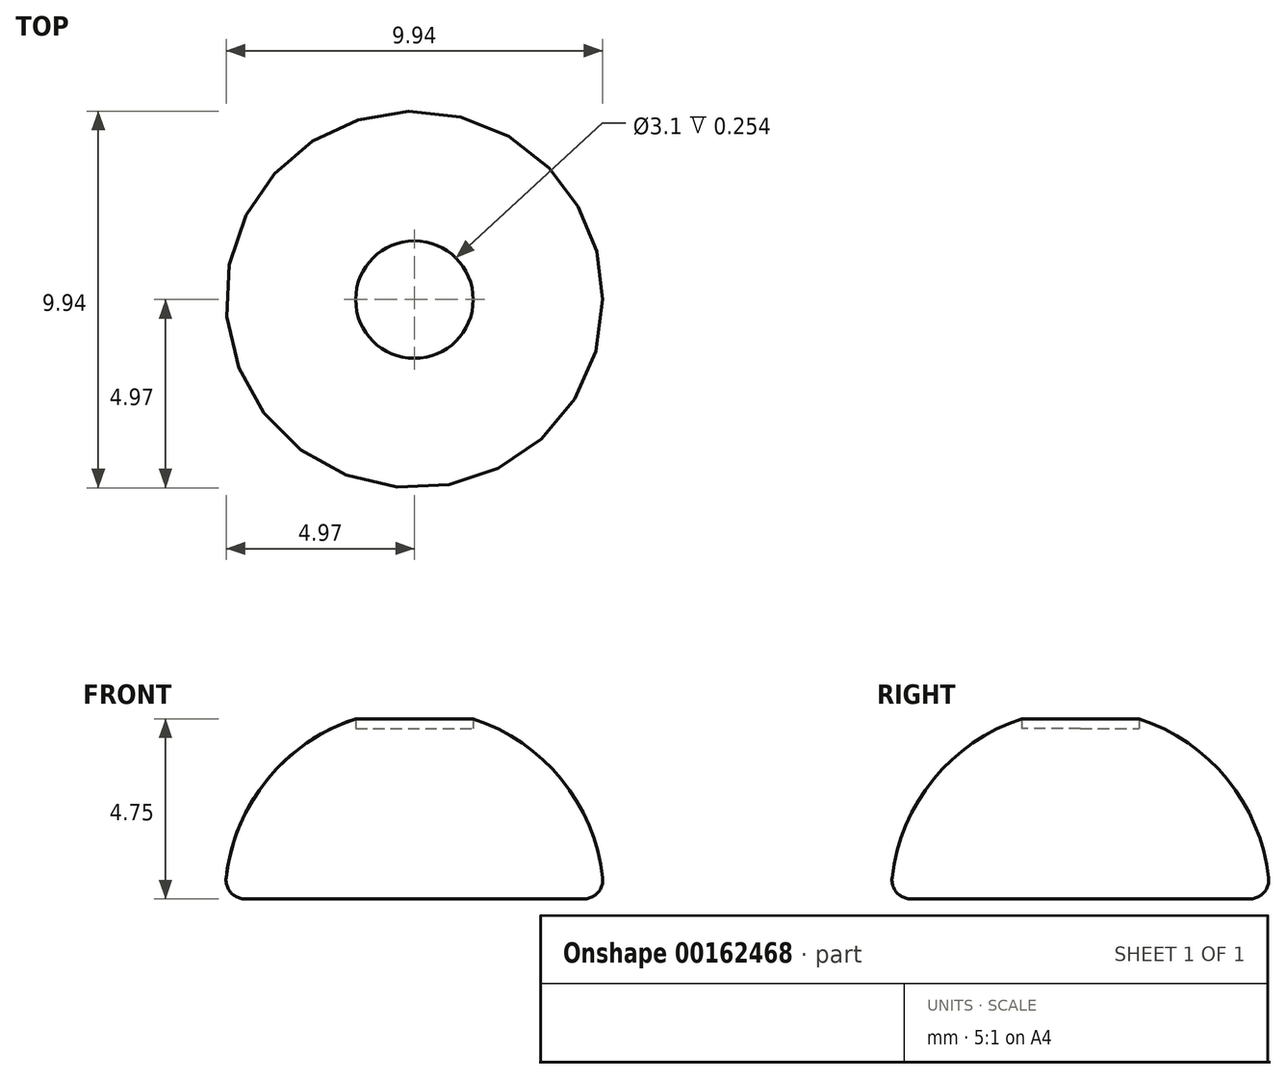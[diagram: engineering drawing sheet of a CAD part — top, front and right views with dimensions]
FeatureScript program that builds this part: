
annotation { "Feature Type Name" : "Feature", "Feature Type Description" : "" }
export const myFeature = defineFeature(function(context is Context, id is Id, definition is map)
    precondition{}
    {
        {
            var Q0;
            Q0=qCreatedBy(makeId("Top.planeOp"),FACE);
            var sketch = newSketch(context, id + "F0", { "sketchPlane" : qUnion([Q0])});
            skCircle(sketch, "E0", {"center": v(0, 0) * mm, "radius": 5 * mm});
            skSolve(sketch);
        }
        {
            var Q0;
            Q0 = qSketchRegion(id + "F0", true);
            extrude(context, id + "F1", {"entities" : qUnion([Q0]), "depth" : 5 * mm});
        }
        {
            var Q0;
            Q0=makeQuery(id+"F1.opExtrude","CAP_EDGE",EDGE,{"disambiguationData":[OSD([sQuery(id+"F0.wireOp",EDGE,"E0")])],"isStart":false});
            fillet(context, id + "F2", {"entities" : qUnion([Q0]), "radius" : 5 * mm, "tangentPropagation" : true, "allowEdgeOverflow" : false});
        }
        {
            var Q0;
            Q0=qCreatedBy(makeId("Top.planeOp"),FACE);
            cPlane(context, id + "F3", {"entities" : qUnion([Q0]), "cplaneType" : CPlaneType.OFFSET, "offset" : 4.5 * mm, "width" : 152.4 * mm, "height" : 152.4 * mm});
        }
        {
            var Q0;
            Q0=qCreatedBy(id+"F3.planeOp",FACE);
            var sketch = newSketch(context, id + "F4", { "sketchPlane" : qUnion([Q0])});
            skCircle(sketch, "E1", {"center": v(0, 0) * mm, "radius": 1.55 * mm});
            skSolve(sketch);
        }
        {
            var Q0;
            Q0 = qSketchRegion(id + "F4", true);
            extrude(context, id + "F5", {"entities" : qUnion([Q0]), "operationType" : NewBodyOperationType.REMOVE, "depth" : 25.4 * mm});
        }
        {
            var Q0;
            {var subQ0=sQuery(id+"F0.wireOp",EDGE,"E0");Q0=makeQuery(id+"F2.opFillet","BLEND_EDGE",EDGE,{"blendedFrom":[makeQuery(id+"F1.opExtrude","CAP_EDGE",EDGE,{"disambiguationData":[OSD([subQ0])],"isStart":false}),makeQuery(id+"F1.opExtrude","CAP_FACE",FACE,{"disambiguationData":[OSD([subQ0])],"isStart":true})],"blendedInto":[makeQuery(id+"F1.opExtrude","CAP_FACE",FACE,{"disambiguationData":[OSD([subQ0])],"isStart":true})]});}
            fillet(context, id + "F6", {"entities" : qUnion([Q0]), "radius" : .5 * mm, "tangentPropagation" : true, "allowEdgeOverflow" : false});
        }
    });
